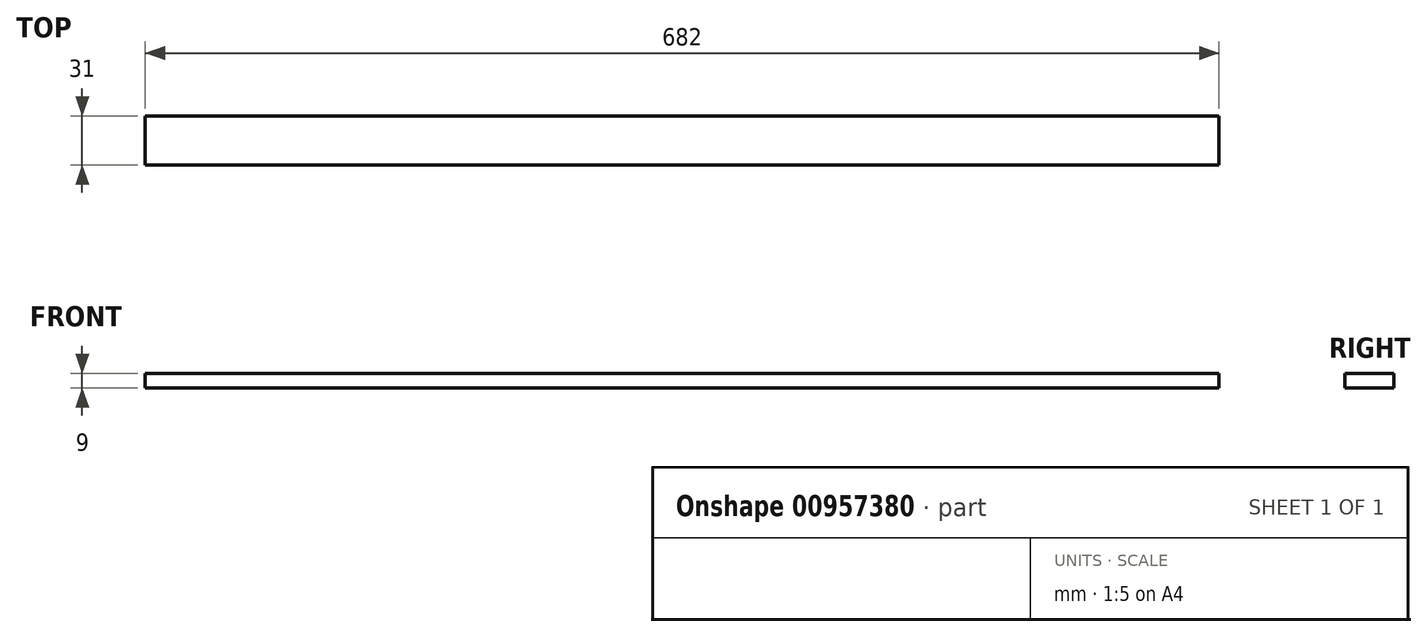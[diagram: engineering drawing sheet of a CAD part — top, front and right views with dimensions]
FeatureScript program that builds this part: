
annotation { "Feature Type Name" : "Feature", "Feature Type Description" : "" }
export const myFeature = defineFeature(function(context is Context, id is Id, definition is map)
    precondition{}
    {
        {
            var Q0;
            Q0=qCreatedBy(makeId("Top.planeOp"),FACE);
            var sketch = newSketch(context, id + "F0", { "sketchPlane" : qUnion([Q0])});
            skLineSegment(sketch, "E0.bottom", {"start": v(341, 15.5) * mm, "end": v(-341, 15.5) * mm});
            skLineSegment(sketch, "E0.top", {"start": v(341, -15.5) * mm, "end": v(-341, -15.5) * mm});
            skLineSegment(sketch, "E0.left", {"start": v(341, 15.5) * mm, "end": v(341, -15.5) * mm});
            skLineSegment(sketch, "E0.right", {"start": v(-341, 15.5) * mm, "end": v(-341, -15.5) * mm});
            skPoint(sketch, "E0.middle", {"position": v(0, 0) * mm});
            skSolve(sketch);
        }
        {
            var Q0;
            Q0=makeQuery(id+"F0.imprint","IMPRINT",FACE,{"disambiguationData":[TD([[makeQuery(id+"F0.imprint","IMPRINT",EDGE,{"derivedFrom":sQuery(id+"F0.wireOp",EDGE,"E0.bottom")}),1.0]])]});
            extrude(context, id + "F1", {"entities" : qUnion([Q0]), "depth" : 9 * mm, "offsetDistance" : 25 * mm});
        }
    });
